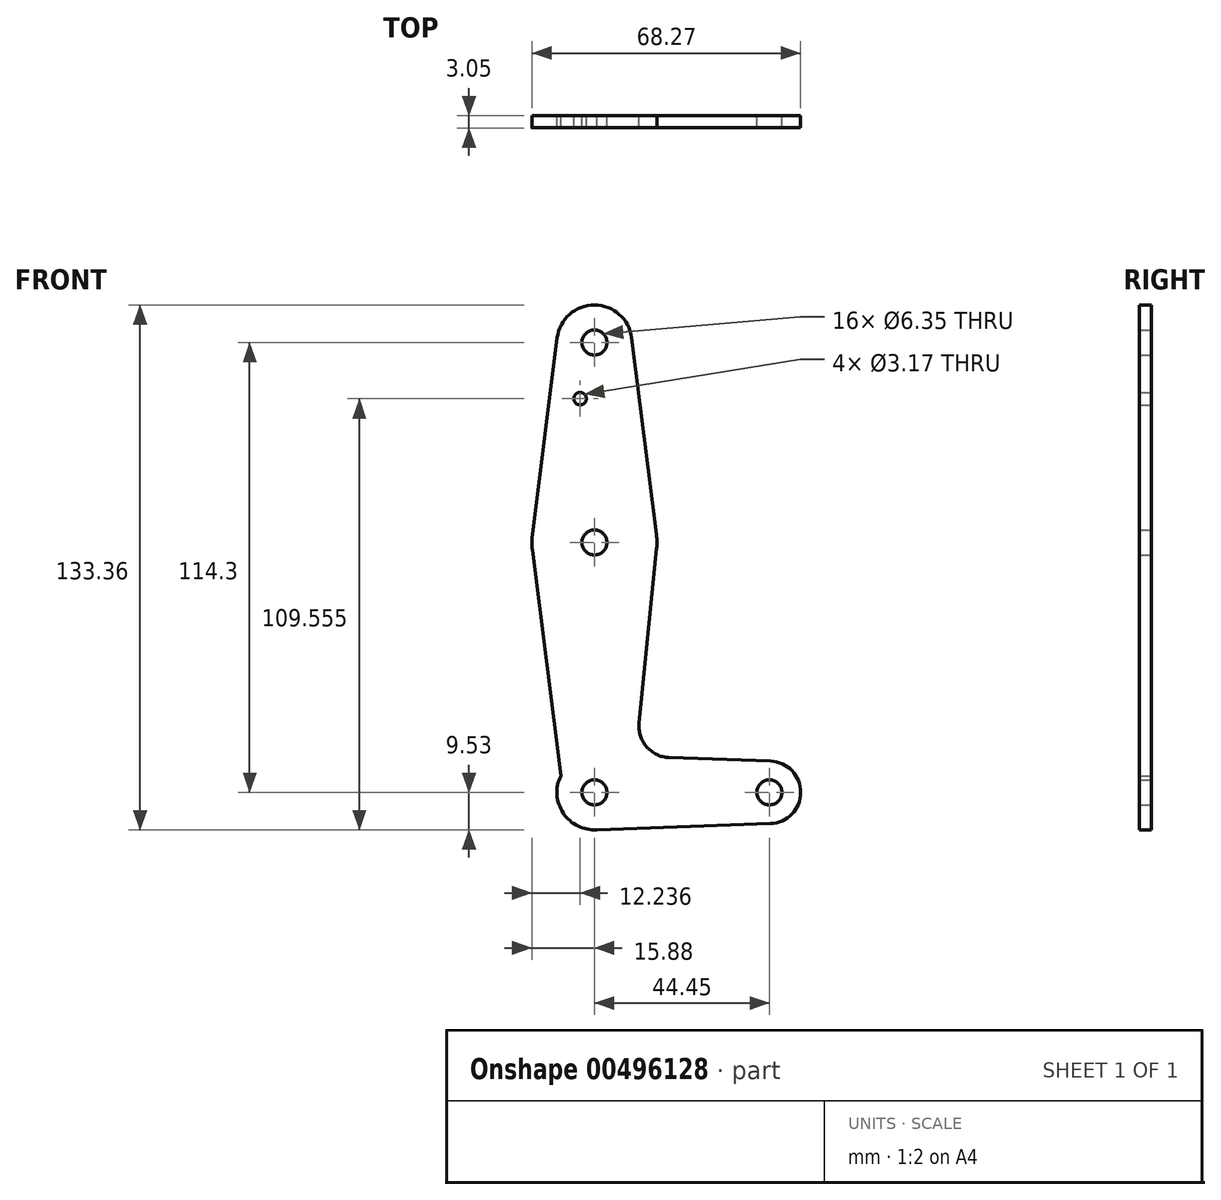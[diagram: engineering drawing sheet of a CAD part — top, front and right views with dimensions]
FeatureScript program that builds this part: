
annotation { "Feature Type Name" : "Feature", "Feature Type Description" : "" }
export const myFeature = defineFeature(function(context is Context, id is Id, definition is map)
    precondition{}
    {
        {
            var Q0;
            Q0=qCreatedBy(makeId("Front.planeOp"),FACE);
            var sketch = newSketch(context, id + "F0", { "sketchPlane" : qUnion([Q0])});
            skLineSegment(sketch, "E0", {"start": v(44.45, 0) * mm, "end": v(0, 0) * mm, "construction": true});
            skLineSegment(sketch, "E1", {"start": v(0, 0) * mm, "end": v(0, 114.3) * mm, "construction": true});
            skCircle(sketch, "E2", {"center": v(0, 114.3) * mm, "radius": 9.53 * mm});
            skCircle(sketch, "E3", {"center": v(0, 0) * mm, "radius": 9.53 * mm});
            skCircle(sketch, "E4", {"center": v(44.45, 0) * mm, "radius": 7.94 * mm});
            skCircle(sketch, "E5", {"center": v(0, 63.5) * mm, "radius": 15.88 * mm});
            skLineSegment(sketch, "E6", {"start": v(-9.45, 115.5) * mm, "end": v(-15.75, 65.48) * mm});
            skLineSegment(sketch, "E7", {"start": v(-15.75, 65.48) * mm, "end": v(-15.75, 61.52) * mm});
            skLineSegment(sketch, "E8", {"start": v(9.45, 115.5) * mm, "end": v(15.75, 65.48) * mm});
            skLineSegment(sketch, "E9", {"start": v(15.75, 65.48) * mm, "end": v(15.75, 61.52) * mm});
            skCircle(sketch, "E10", {"center": v(0, 114.3) * mm, "radius": 3.18 * mm});
            skCircle(sketch, "E11", {"center": v(0, 63.5) * mm, "radius": 3.18 * mm});
            skCircle(sketch, "E12", {"center": v(0, 0) * mm, "radius": 3.18 * mm});
            skCircle(sketch, "E13", {"center": v(44.45, 0) * mm, "radius": 3.18 * mm});
            skCircle(sketch, "E14", {"center": v(-3.64, 100.03) * mm, "radius": 1.59 * mm});
            skPoint(sketch, "E15.newPointA", {"position": v(9.57, 0) * mm});
            skLineSegment(sketch, "E16", {"start": v(0, -9.53) * mm, "end": v(44.73, -7.93) * mm});
            skLineSegment(sketch, "E17", {"start": v(15.8, 61.91) * mm, "end": v(11.34, 17.6) * mm});
            skLineSegment(sketch, "E18", {"start": v(44.73, 7.93) * mm, "end": v(18.97, 8.85) * mm});
            skArc(sketch, "E19.filletArc", {"start": v(11.34, 17.6) * mm, "mid": v(13.26, 11.57) * mm, "end": v(18.97, 8.85) * mm});
            skLineSegment(sketch, "E20", {"start": v(-8.53, 4.23) * mm, "end": v(-15.75, 61.52) * mm});
            skSolve(sketch);
        }
        {
            var Q0;
            Q0 = qSketchRegion(id + "F0", true);
            extrude(context, id + "F1", {"entities" : qUnion([Q0]), "depth" : 3.05 * mm});
        }
    });
